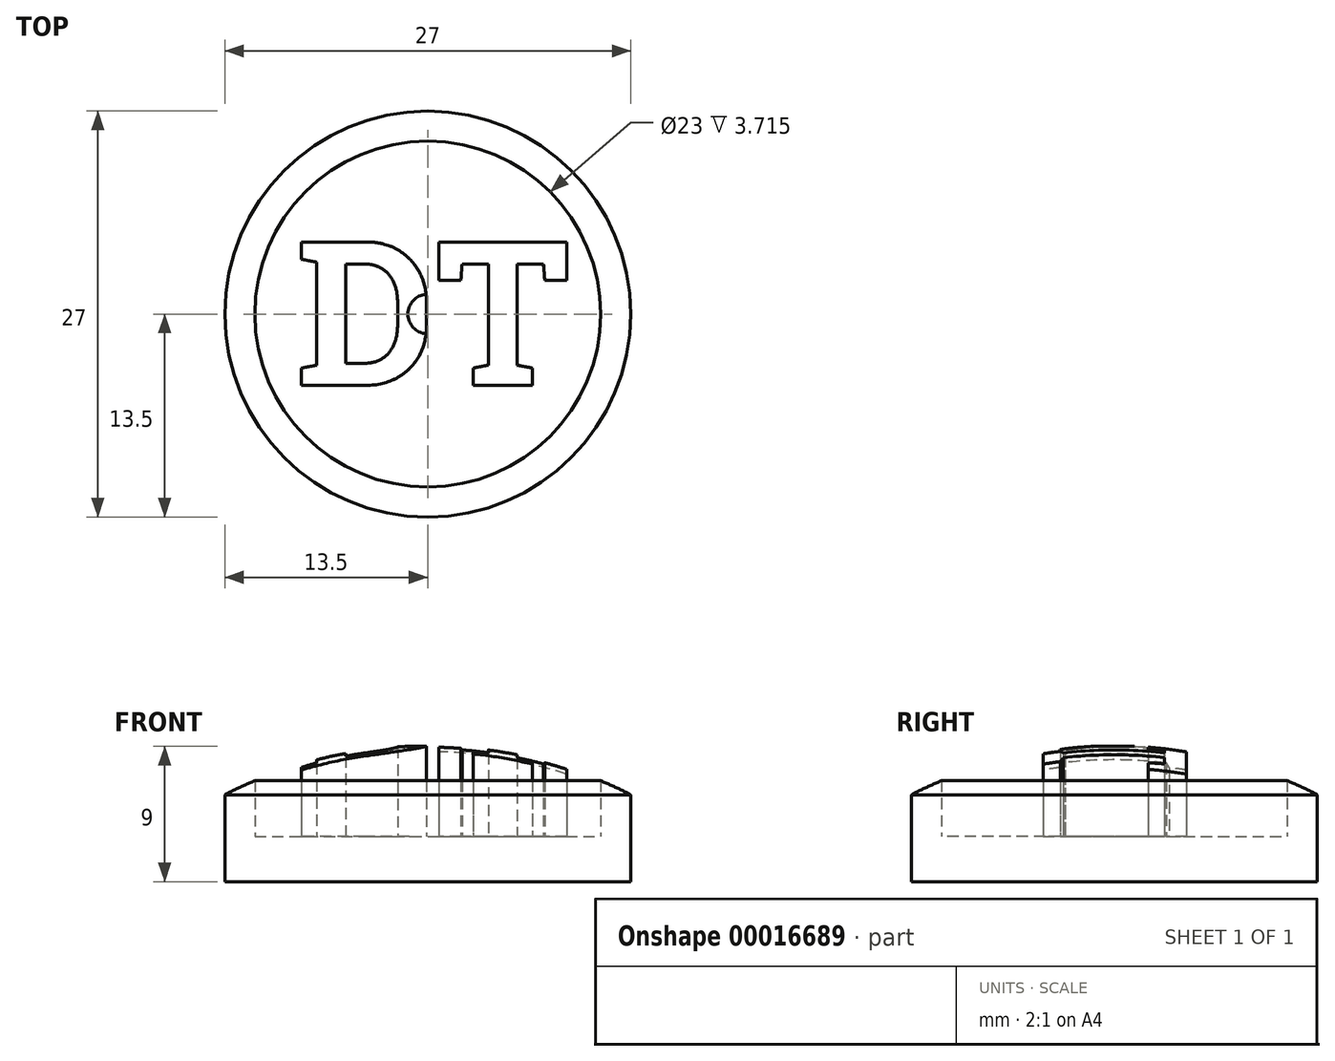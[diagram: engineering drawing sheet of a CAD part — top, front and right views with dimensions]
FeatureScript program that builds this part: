
annotation { "Feature Type Name" : "Feature", "Feature Type Description" : "" }
export const myFeature = defineFeature(function(context is Context, id is Id, definition is map)
    precondition{}
    {
        {
            var Q0;
            Q0=qCreatedBy(makeId("Top.planeOp"),FACE);
            var sketch = newSketch(context, id + "F0", { "sketchPlane" : qUnion([Q0])});
            skCircle(sketch, "E0", {"center": v(0, 0) * mm, "radius": 13.5 * mm});
            skCircle(sketch, "E1.0", {"center": v(0, 0) * mm, "radius": 11.5 * mm});
            skText(sketch, "E2", { "text": "DT", "fontName": "RobotoSlab-Bold.ttf"});
            const initialGuessF0  = {"E2": [-0.00876, -0.00474, 1, 0, 0.00966]};
            skSetInitialGuess(sketch, initialGuessF0);
            skSolve(sketch);
        }
        {
            var Q0;
            Q0=makeQuery(id+"F0.imprint","IMPRINT",FACE,{"disambiguationData":[TD([[makeQuery(id+"F0.imprint","IMPRINT",EDGE,{"derivedFrom":sQuery(id+"F0.wireOp",EDGE,"E0")}),1.0]])]});
            var Q1;
            Q1=makeQuery(id+"F0.imprint","IMPRINT",FACE,{"disambiguationData":[TD([[makeQuery(id+"F0.imprint","IMPRINT",EDGE,{"derivedFrom":sQuery(id+"F0.wireOp",EDGE,"E2.sketch_text.stroke-0")}),-1.0]])]});
            var Q2;
            Q2=makeQuery(id+"F0.imprint","IMPRINT",FACE,{"disambiguationData":[TD([[makeQuery(id+"F0.imprint","IMPRINT",EDGE,{"derivedFrom":sQuery(id+"F0.wireOp",EDGE,"E2.sketch_text.stroke-21")}),-1.0]])]});
            extrude(context, id + "F1", {"entities" : qUnion([Q0, Q1, Q2]), "depth" : 6 * mm});
        }
        {
            var Q0;
            Q0=qCreatedBy(makeId("Top.planeOp"),FACE);
            var sketch = newSketch(context, id + "F2", { "sketchPlane" : qUnion([Q0])});
            skCircle(sketch, "E3", {"center": v(0, 0) * mm, "radius": 13.5 * mm});
            skSolve(sketch);
        }
        {
            var Q0;
            Q0 = qSketchRegion(id + "F2", true);
            extrude(context, id + "F3", {"entities" : qUnion([Q0]), "operationType" : NewBodyOperationType.ADD, "oppositeDirection" : true, "depth" : 3 * mm});
        }
        {
            var Q0;
            Q0=qCreatedBy(makeId("Front.planeOp"),FACE);
            var sketch = newSketch(context, id + "F4", { "sketchPlane" : qUnion([Q0])});
            skArc(sketch, "E4", {"start": v(0, 6.03) * mm, "mid": v(-6.98, 5.2) * mm, "end": v(-13.57, 2.75) * mm});
            skLineSegment(sketch, "E5", {"start": v(-13.57, 2.75) * mm, "end": v(-13.57, 10.07) * mm});
            skLineSegment(sketch, "E6", {"start": v(-13.57, 10.07) * mm, "end": v(0, 10.07) * mm});
            skLineSegment(sketch, "E7", {"start": v(0, 10.07) * mm, "end": v(0, 6.03) * mm});
            skSolve(sketch);
        }
        {
            var Q0;
            Q0 = qSketchRegion(id + "F4", true);
            var Q1;
            Q1=sQuery(id+"F4.wireOp",EDGE,"E7");
            revolve(context, id + "F5", {"operationType" : NewBodyOperationType.REMOVE, "entities" : qUnion([Q0]), "axis" : qUnion([Q1]), "revolveType" : RevolveType.FULL, "oppositeDirection" : true});
        }
    });
